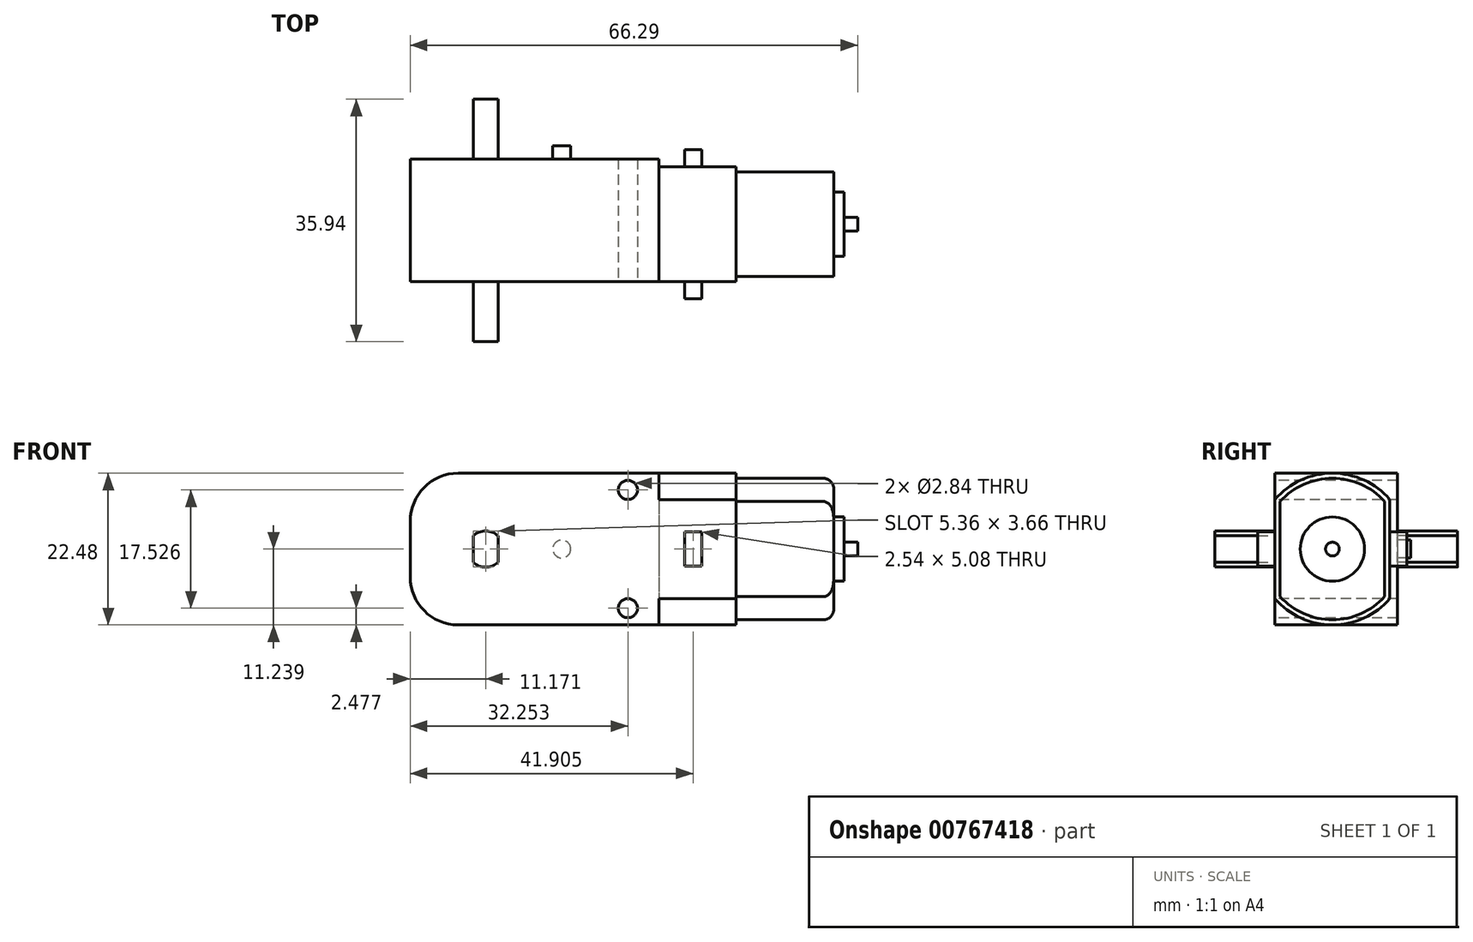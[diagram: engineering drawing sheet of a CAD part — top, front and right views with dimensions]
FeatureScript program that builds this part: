
annotation { "Feature Type Name" : "Feature", "Feature Type Description" : "" }
export const myFeature = defineFeature(function(context is Context, id is Id, definition is map)
    precondition{}
    {
        {
            var Q0;
            Q0=qCreatedBy(makeId("Top.planeOp"),FACE);
            var sketch = newSketch(context, id + "F0", { "sketchPlane" : qUnion([Q0])});
            skLineSegment(sketch, "E0.bottom", {"start": v(49.21, -49.21) * mm, "end": v(-49.21, -49.21) * mm, "construction": true});
            skLineSegment(sketch, "E0.top", {"start": v(49.21, 49.21) * mm, "end": v(-49.21, 49.21) * mm, "construction": true});
            skLineSegment(sketch, "E0.left", {"start": v(49.21, -49.21) * mm, "end": v(49.21, 49.21) * mm, "construction": true});
            skLineSegment(sketch, "E0.right", {"start": v(-49.21, -49.21) * mm, "end": v(-49.21, 49.21) * mm, "construction": true});
            skPoint(sketch, "E0.middle", {"position": v(0, 0) * mm});
            skLineSegment(sketch, "E1", {"start": v(-35.05, -0.76) * mm, "end": v(35.05, -0.76) * mm, "construction": true});
            skLineSegment(sketch, "E2", {"start": v(0, 11.11) * mm, "end": v(0, -11.11) * mm, "construction": true});
            skLineSegment(sketch, "E3", {"start": v(-18.41, 7.75) * mm, "end": v(18.42, 7.75) * mm});
            skLineSegment(sketch, "E4.MirrorCS", {"start": v(-18.41, -9.27) * mm, "end": v(18.41, -9.27) * mm});
            skLineSegment(sketch, "E5", {"start": v(18.42, 7.75) * mm, "end": v(18.42, -9.27) * mm});
            skLineSegment(sketch, "E6.MirrorCS", {"start": v(-18.42, 7.75) * mm, "end": v(-18.41, -9.27) * mm});
            skPoint(sketch, "E7.orphan", {"position": v(12.01, 7.75) * mm});
            skPoint(sketch, "E8.orphan", {"position": v(12.01, -9.27) * mm});
            skPoint(sketch, "E9.orphan", {"position": v(18.42, -26.12) * mm});
            skPoint(sketch, "E10.orphan", {"position": v(-18.41, -26.12) * mm});
            skPoint(sketch, "E11.orphan", {"position": v(-32.46, 7.75) * mm});
            skPoint(sketch, "E12.orphan", {"position": v(-18.42, 15.48) * mm});
            skPoint(sketch, "E13.orphan", {"position": v(18.41, 15.48) * mm});
            skPoint(sketch, "E14.orphan", {"position": v(-32.46, -9.27) * mm});
            skSolve(sketch);
        }
        {
            var Q0;
            Q0=makeQuery(id+"F0.imprint","IMPRINT",FACE,{"disambiguationData":[TD([[makeQuery(id+"F0.imprint","IMPRINT",EDGE,{"derivedFrom":sQuery(id+"F0.wireOp",EDGE,"E3")}),-1.0]])]});
            extrude(context, id + "F1", {"entities" : qUnion([Q0]), "depth" : 22.48 * mm});
        }
        {
            var Q0;
            Q0=makeQuery(id+"F1.opExtrude","CAP_EDGE",EDGE,{"disambiguationData":[OSD([sQuery(id+"F0.wireOp",EDGE,"E6.MirrorCS")])],"isStart":false});
            var Q1;
            Q1=makeQuery(id+"F1.opExtrude","CAP_EDGE",EDGE,{"disambiguationData":[OSD([sQuery(id+"F0.wireOp",EDGE,"E6.MirrorCS")])],"isStart":true});
            fillet(context, id + "F2", {"entities" : qUnion([Q0, Q1]), "radius" : 7.11 * mm, "tangentPropagation" : true, "allowEdgeOverflow" : false});
        }
        {
            var Q0;
            Q0=makeQuery(id+"F1.opExtrude","SWEPT_FACE",FACE,{"disambiguationData":[OSD([sQuery(id+"F0.wireOp",EDGE,"E5")])]});
            var sketch = newSketch(context, id + "F3", { "sketchPlane" : qUnion([Q0])});
            skLineSegment(sketch, "E15", {"start": v(-9.27, 11.24) * mm, "end": v(7.75, 11.24) * mm, "construction": true});
            skArc(sketch, "E16", {"start": v(-9.27, 3.9) * mm, "mid": v(-0.76, 0) * mm, "end": v(7.75, 3.9) * mm});
            skLineSegment(sketch, "E17.0", {"start": v(-9.27, 18.58) * mm, "end": v(-9.27, 3.9) * mm});
            skLineSegment(sketch, "E18.0", {"start": v(7.75, 18.58) * mm, "end": v(7.75, 3.9) * mm});
            skPoint(sketch, "E19.orphan", {"position": v(-9.27, 22.48) * mm});
            skPoint(sketch, "E20.orphan", {"position": v(7.75, 22.48) * mm});
            skArc(sketch, "E21.trimOffspring", {"start": v(7.75, 18.58) * mm, "mid": v(-0.76, 22.48) * mm, "end": v(-9.27, 18.58) * mm});
            skPoint(sketch, "E22.orphan", {"position": v(7.75, 0) * mm});
            skPoint(sketch, "E23.orphan", {"position": v(-9.27, 0) * mm});
            skSolve(sketch);
        }
        {
            var Q0;
            {var subQ1=sQuery(id+"F3.wireOp",EDGE,"E17.0");Q0=makeQuery(id+"F3.imprint","IMPRINT",FACE,{"disambiguationData":[TD([[makeQuery(id+"F3.imprint","IMPRINT",EDGE,{"derivedFrom":subQ1}),1.0]])]});}
            var Q1;
            Q1=makeQuery(id+"F1.opExtrude","SWEPT_FACE",FACE,{"disambiguationData":[OSD([sQuery(id+"F0.wireOp",EDGE,"E6.MirrorCS")])]});
            extrude(context, id + "F4", {"entities" : qUnion([Q0, Q1]), "operationType" : NewBodyOperationType.ADD, "depth" : 27.43 * mm});
        }
        {
            var Q0;
            Q0=makeQuery(id+"F4.opExtrude","CAP_FACE",FACE,{"disambiguationData":[OSD([sQuery(id+"F3.wireOp",EDGE,"E16"),sQuery(id+"F3.wireOp",EDGE,"E17.0"),sQuery(id+"F3.wireOp",EDGE,"E18.0"),sQuery(id+"F3.wireOp",EDGE,"E21.trimOffspring")])],"isStart":false});
            var sketch = newSketch(context, id + "F5", { "sketchPlane" : qUnion([Q0])});
            skLineSegment(sketch, "E24.0", {"start": v(-8.5, 18.3) * mm, "end": v(-8.5, 4.19) * mm});
            skArc(sketch, "E24.1", {"start": v(6.99, 18.3) * mm, "mid": v(-0.76, 21.72) * mm, "end": v(-8.5, 18.3) * mm});
            skLineSegment(sketch, "E24.2", {"start": v(6.99, 4.19) * mm, "end": v(6.99, 18.3) * mm});
            skArc(sketch, "E24.3", {"start": v(-8.5, 4.19) * mm, "mid": v(-0.76, 0.76) * mm, "end": v(6.99, 4.19) * mm});
            skLineSegment(sketch, "E25.0", {"start": v(-14.86, 20.43) * mm, "end": v(-14.86, 2.05) * mm});
            skArc(sketch, "E25.1", {"start": v(13.34, 20.43) * mm, "mid": v(-0.76, 28.07) * mm, "end": v(-14.86, 20.43) * mm});
            skLineSegment(sketch, "E25.2", {"start": v(13.34, 2.05) * mm, "end": v(13.34, 20.43) * mm});
            skArc(sketch, "E25.3", {"start": v(-14.86, 2.05) * mm, "mid": v(-0.76, -5.59) * mm, "end": v(13.34, 2.05) * mm});
            skSolve(sketch);
        }
        {
            var Q0;
            Q0=makeQuery(id+"F5.imprint","IMPRINT",FACE,{"disambiguationData":[TD([[makeQuery(id+"F5.imprint","IMPRINT",EDGE,{"derivedFrom":sQuery(id+"F5.wireOp",EDGE,"E25.0")}),1.0]])]});
            var Q1;
            Q1=makeQuery(id+"F5.imprint","IMPRINT",FACE,{"disambiguationData":[TD([[makeQuery(id+"F5.imprint","IMPRINT",EDGE,{"derivedFrom":sQuery(id+"F5.wireOp",EDGE,"E24.0")}),-1.0]])]});
            extrude(context, id + "F6", {"entities" : qUnion([Q0, Q1]), "operationType" : NewBodyOperationType.REMOVE, "oppositeDirection" : true, "depth" : 16 * mm});
        }
        {
            var Q0;
            Q0=makeQuery(id+"F4.opExtrude","CAP_FACE",FACE,{"disambiguationData":[OSD([sQuery(id+"F3.wireOp",EDGE,"E16"),sQuery(id+"F3.wireOp",EDGE,"E17.0"),sQuery(id+"F3.wireOp",EDGE,"E18.0"),sQuery(id+"F3.wireOp",EDGE,"E21.trimOffspring")])],"isStart":false});
            var sketch = newSketch(context, id + "F7", { "sketchPlane" : qUnion([Q0])});
            skCircle(sketch, "E26", {"center": v(-0.76, 11.24) * mm, "radius": 4.76 * mm});
            skCircle(sketch, "E27", {"center": v(-0.76, 11.24) * mm, "radius": 12.82 * mm});
            skSolve(sketch);
        }
        {
            var Q0;
            Q0=makeQuery(id+"F7.imprint","IMPRINT",FACE,{"disambiguationData":[TD([[makeQuery(id+"F7.imprint","IMPRINT",EDGE,{"derivedFrom":sQuery(id+"F7.wireOp",EDGE,"E27")}),1.0]])]});
            var Q1;
            Q1=makeQuery(id+"F7.imprint","IMPRINT",FACE,{"disambiguationData":[TD([[makeQuery(id+"F7.imprint","IMPRINT",EDGE,{"derivedFrom":sQuery(id+"F7.wireOp",EDGE,"E26")}),-1.0]])]});
            extrude(context, id + "F8", {"entities" : qUnion([Q0, Q1]), "operationType" : NewBodyOperationType.REMOVE, "oppositeDirection" : true, "depth" : 1.52 * mm});
        }
        {
            var Q0;
            Q0=makeQuery(id+"F8.boolean.opBoolean","INTERSECT",EDGE,{"derivedFrom":[makeQuery(id+"F6.boolean.opBoolean","COPY",FACE,{"derivedFrom":makeQuery(id+"F6.opExtrude","SWEPT_FACE",FACE,{"disambiguationData":[OSD([sQuery(id+"F5.wireOp",EDGE,"E24.3")])]})}),makeQuery(id+"F8.opExtrude","CAP_FACE",FACE,{"disambiguationData":[OSD([sQuery(id+"F7.wireOp",EDGE,"E26"),sQuery(id+"F7.wireOp",EDGE,"E27")])],"isStart":false})]});
            var Q1;
            Q1=makeQuery(id+"F8.boolean.opBoolean","INTERSECT",EDGE,{"derivedFrom":[makeQuery(id+"F6.boolean.opBoolean","COPY",FACE,{"derivedFrom":makeQuery(id+"F6.opExtrude","SWEPT_FACE",FACE,{"disambiguationData":[OSD([sQuery(id+"F5.wireOp",EDGE,"E24.1")])]})}),makeQuery(id+"F8.opExtrude","CAP_FACE",FACE,{"disambiguationData":[OSD([sQuery(id+"F7.wireOp",EDGE,"E26"),sQuery(id+"F7.wireOp",EDGE,"E27")])],"isStart":false})]});
            fillet(context, id + "F9", {"entities" : qUnion([Q0, Q1]), "radius" : 1.52 * mm, "tangentPropagation" : true, "allowEdgeOverflow" : false});
        }
        {
            var Q0;
            Q0=makeQuery(id+"F4.opExtrude","CAP_FACE",FACE,{"disambiguationData":[OSD([sQuery(id+"F3.wireOp",EDGE,"E16"),sQuery(id+"F3.wireOp",EDGE,"E17.0"),sQuery(id+"F3.wireOp",EDGE,"E18.0"),sQuery(id+"F3.wireOp",EDGE,"E21.trimOffspring")])],"isStart":false});
            var sketch = newSketch(context, id + "F10", { "sketchPlane" : qUnion([Q0])});
            skCircle(sketch, "E28", {"center": v(-0.76, 11.24) * mm, "radius": 1.02 * mm});
            skSolve(sketch);
        }
        {
            var Q0;
            Q0=makeQuery(id+"F10.imprint","IMPRINT",FACE,{"disambiguationData":[TD([[makeQuery(id+"F10.imprint","IMPRINT",EDGE,{"derivedFrom":sQuery(id+"F10.wireOp",EDGE,"E28")}),1.0]])]});
            extrude(context, id + "F11", {"entities" : qUnion([Q0]), "operationType" : NewBodyOperationType.ADD, "depth" : 2.03 * mm});
        }
        {
            var Q0;
            Q0=makeQuery(id+"F4.boolean.opBoolean","MERGE",FACE,{"derivedFrom":[makeQuery(id+"F1.opExtrude","SWEPT_FACE",FACE,{"disambiguationData":[OSD([sQuery(id+"F0.wireOp",EDGE,"E4.MirrorCS")])]}),makeQuery(id+"F4.opExtrude","SWEPT_FACE",FACE,{"disambiguationData":[OSD([sQuery(id+"F3.wireOp",EDGE,"E17.0")])]})]});
            var sketch = newSketch(context, id + "F12", { "sketchPlane" : qUnion([Q0])});
            skLineSegment(sketch, "E29", {"start": v(29.85, 11.24) * mm, "end": v(18.51, 11.24) * mm, "construction": true});
            skLineSegment(sketch, "E30", {"start": v(22.23, 13.78) * mm, "end": v(22.23, 8.7) * mm});
            skLineSegment(sketch, "E31", {"start": v(24.77, 13.78) * mm, "end": v(24.77, 8.7) * mm});
            skLineSegment(sketch, "E32", {"start": v(22.23, 13.78) * mm, "end": v(24.77, 13.78) * mm});
            skLineSegment(sketch, "E33.MirrorCS", {"start": v(22.23, 8.7) * mm, "end": v(24.77, 8.7) * mm});
            skPoint(sketch, "E34.orphan", {"position": v(19.69, 8.7) * mm});
            skPoint(sketch, "E35.orphan", {"position": v(27.19, 8.7) * mm});
            skPoint(sketch, "E36.orphan", {"position": v(27.19, 13.78) * mm});
            skPoint(sketch, "E37.orphan", {"position": v(19.69, 13.78) * mm});
            skSolve(sketch);
        }
        {
            var Q0;
            Q0=makeQuery(id+"F12.imprint","IMPRINT",FACE,{"disambiguationData":[TD([[makeQuery(id+"F12.imprint","IMPRINT",EDGE,{"derivedFrom":sQuery(id+"F12.wireOp",EDGE,"E30")}),1.0]])]});
            extrude(context, id + "F13", {"entities" : qUnion([Q0]), "operationType" : NewBodyOperationType.ADD, "depth" : 2.54 * mm});
        }
        {
            var Q0;
            Q0=makeQuery(id+"F4.boolean.opBoolean","MERGE",FACE,{"derivedFrom":[makeQuery(id+"F1.opExtrude","SWEPT_FACE",FACE,{"disambiguationData":[OSD([sQuery(id+"F0.wireOp",EDGE,"E3")])]}),makeQuery(id+"F4.opExtrude","SWEPT_FACE",FACE,{"disambiguationData":[OSD([sQuery(id+"F3.wireOp",EDGE,"E18.0")])]})]});
            var sketch = newSketch(context, id + "F14", { "sketchPlane" : qUnion([Q0])});
            skLineSegment(sketch, "E38.0", {"start": v(11.3, 0) * mm, "end": v(-18.42, 0) * mm});
            skArc(sketch, "E39.0", {"start": v(11.3, 0) * mm, "mid": v(16.33, 2.08) * mm, "end": v(18.41, 7.11) * mm});
            skLineSegment(sketch, "E40.0", {"start": v(18.42, 15.37) * mm, "end": v(18.42, 7.11) * mm});
            skArc(sketch, "E41.0", {"start": v(18.41, 15.37) * mm, "mid": v(16.33, 20.4) * mm, "end": v(11.3, 22.48) * mm});
            skLineSegment(sketch, "E42.0", {"start": v(11.3, 22.48) * mm, "end": v(-18.42, 22.48) * mm});
            skLineSegment(sketch, "E43", {"start": v(-18.42, 22.48) * mm, "end": v(-18.42, 0) * mm});
            skSolve(sketch);
        }
        {
            var Q0;
            {var subQ0=sQuery(id+"F14.wireOp",EDGE,"E38.0");Q0=makeQuery(id+"F14.imprint","IMPRINT",FACE,{"disambiguationData":[TD([[makeQuery(id+"F14.imprint","IMPRINT",EDGE,{"derivedFrom":subQ0}),-1.0]])]});}
            extrude(context, id + "F15", {"entities" : qUnion([Q0]), "operationType" : NewBodyOperationType.ADD, "depth" : 1.14 * mm});
        }
        {
            var Q0;
            Q0=makeQuery(id+"F4.boolean.opBoolean","MERGE",FACE,{"derivedFrom":[makeQuery(id+"F1.opExtrude","SWEPT_FACE",FACE,{"disambiguationData":[OSD([sQuery(id+"F0.wireOp",EDGE,"E3")])]}),makeQuery(id+"F4.opExtrude","SWEPT_FACE",FACE,{"disambiguationData":[OSD([sQuery(id+"F3.wireOp",EDGE,"E18.0")])]})]});
            var sketch = newSketch(context, id + "F16", { "sketchPlane" : qUnion([Q0])});
            skLineSegment(sketch, "E44.0.0", {"start": v(-24.77, 13.78) * mm, "end": v(-22.23, 13.78) * mm});
            skLineSegment(sketch, "E44.0.1", {"start": v(-22.23, 13.78) * mm, "end": v(-22.23, 8.7) * mm});
            skLineSegment(sketch, "E44.0.2", {"start": v(-22.23, 8.7) * mm, "end": v(-24.77, 8.7) * mm});
            skLineSegment(sketch, "E44.0.3", {"start": v(-24.77, 8.7) * mm, "end": v(-24.77, 13.78) * mm});
            skSolve(sketch);
        }
        {
            var Q0;
            Q0=makeQuery(id+"F16.imprint","IMPRINT",FACE,{"disambiguationData":[TD([[makeQuery(id+"F16.imprint","IMPRINT",EDGE,{"derivedFrom":sQuery(id+"F16.wireOp",EDGE,"E44.0.0")}),-1.0]])]});
            extrude(context, id + "F17", {"entities" : qUnion([Q0]), "operationType" : NewBodyOperationType.ADD, "depth" : 2.54 * mm});
        }
        {
            var Q0;
            Q0=makeQuery(id+"F4.boolean.opBoolean","MERGE",FACE,{"derivedFrom":[makeQuery(id+"F1.opExtrude","SWEPT_FACE",FACE,{"disambiguationData":[OSD([sQuery(id+"F0.wireOp",EDGE,"E4.MirrorCS")])]}),makeQuery(id+"F4.opExtrude","SWEPT_FACE",FACE,{"disambiguationData":[OSD([sQuery(id+"F3.wireOp",EDGE,"E17.0")])]})]});
            var sketch = newSketch(context, id + "F18", { "sketchPlane" : qUnion([Q0])});
            skArc(sketch, "E45", {"start": v(-5.41, 13.2) * mm, "mid": v(-7.24, 13.92) * mm, "end": v(-9.07, 13.2) * mm});
            skPoint(sketch, "E45.centerSnap0", {"position": v(-18.41, 11.24) * mm});
            skLineSegment(sketch, "E46", {"start": v(-9.07, 13.2) * mm, "end": v(-9.07, 9.28) * mm});
            skLineSegment(sketch, "E47", {"start": v(-5.41, 13.2) * mm, "end": v(-5.41, 9.28) * mm});
            skPoint(sketch, "E48.orphan", {"position": v(-9.07, 5.55) * mm});
            skArc(sketch, "E49.trimOffspring", {"start": v(-9.07, 9.28) * mm, "mid": v(-7.24, 8.56) * mm, "end": v(-5.41, 9.28) * mm});
            skSolve(sketch);
        }
        {
            var Q0;
            Q0=makeQuery(id+"F18.imprint","IMPRINT",FACE,{"disambiguationData":[TD([[makeQuery(id+"F18.imprint","IMPRINT",EDGE,{"derivedFrom":sQuery(id+"F18.wireOp",EDGE,"E45")}),1.0]])]});
            extrude(context, id + "F19", {"entities" : qUnion([Q0]), "operationType" : NewBodyOperationType.ADD, "depth" : 8.9 * mm});
        }
        {
            var Q0;
            Q0=makeQuery(id+"F15.opExtrude","CAP_FACE",FACE,{"disambiguationData":[OSD([sQuery(id+"F14.wireOp",EDGE,"E38.0"),sQuery(id+"F14.wireOp",EDGE,"E39.0"),sQuery(id+"F14.wireOp",EDGE,"E40.0"),sQuery(id+"F14.wireOp",EDGE,"E41.0"),sQuery(id+"F14.wireOp",EDGE,"E42.0"),sQuery(id+"F14.wireOp",EDGE,"E43")])],"isStart":false});
            var sketch = newSketch(context, id + "F20", { "sketchPlane" : qUnion([Q0])});
            skLineSegment(sketch, "E50.0.0", {"start": v(5.41, 9.28) * mm, "end": v(5.41, 13.2) * mm});
            skArc(sketch, "E50.0.1", {"start": v(5.41, 13.2) * mm, "mid": v(7.24, 13.92) * mm, "end": v(9.07, 13.2) * mm});
            skLineSegment(sketch, "E50.0.2", {"start": v(9.07, 13.2) * mm, "end": v(9.07, 9.28) * mm});
            skArc(sketch, "E50.0.3", {"start": v(9.07, 9.28) * mm, "mid": v(7.24, 8.56) * mm, "end": v(5.41, 9.28) * mm});
            skSolve(sketch);
        }
        {
            var Q0;
            Q0=makeQuery(id+"F20.imprint","IMPRINT",FACE,{"disambiguationData":[TD([[makeQuery(id+"F20.imprint","IMPRINT",EDGE,{"derivedFrom":sQuery(id+"F20.wireOp",EDGE,"E50.0.0")}),-1.0]])]});
            extrude(context, id + "F21", {"entities" : qUnion([Q0]), "operationType" : NewBodyOperationType.ADD, "depth" : 8.9 * mm});
        }
        {
            var Q0;
            Q0=makeQuery(id+"F15.opExtrude","CAP_FACE",FACE,{"disambiguationData":[OSD([sQuery(id+"F14.wireOp",EDGE,"E38.0"),sQuery(id+"F14.wireOp",EDGE,"E39.0"),sQuery(id+"F14.wireOp",EDGE,"E40.0"),sQuery(id+"F14.wireOp",EDGE,"E41.0"),sQuery(id+"F14.wireOp",EDGE,"E42.0"),sQuery(id+"F14.wireOp",EDGE,"E43")])],"isStart":false});
            var sketch = newSketch(context, id + "F22", { "sketchPlane" : qUnion([Q0])});
            skLineSegment(sketch, "E51", {"start": v(7.24, 13.92) * mm, "end": v(7.24, 8.56) * mm, "construction": true});
            skLineSegment(sketch, "E52", {"start": v(-4.04, 11.24) * mm, "end": v(-4.04, 17.91) * mm, "construction": true});
            skLineSegment(sketch, "E53", {"start": v(18.42, 11.24) * mm, "end": v(0, 11.24) * mm, "construction": true});
            skCircle(sketch, "E54", {"center": v(-4.04, 11.24) * mm, "radius": 1.32 * mm});
            skSolve(sketch);
        }
        {
            var Q0;
            Q0=makeQuery(id+"F22.imprint","IMPRINT",FACE,{"disambiguationData":[TD([[makeQuery(id+"F22.imprint","IMPRINT",EDGE,{"derivedFrom":sQuery(id+"F22.wireOp",EDGE,"E54")}),1.0]])]});
            extrude(context, id + "F23", {"entities" : qUnion([Q0]), "operationType" : NewBodyOperationType.ADD, "depth" : 1.96 * mm});
        }
        {
            var Q0;
            Q0=makeQuery(id+"F4.boolean.opBoolean","MERGE",FACE,{"derivedFrom":[makeQuery(id+"F1.opExtrude","SWEPT_FACE",FACE,{"disambiguationData":[OSD([sQuery(id+"F0.wireOp",EDGE,"E4.MirrorCS")])]}),makeQuery(id+"F4.opExtrude","SWEPT_FACE",FACE,{"disambiguationData":[OSD([sQuery(id+"F3.wireOp",EDGE,"E17.0")])]})]});
            var sketch = newSketch(context, id + "F24", { "sketchPlane" : qUnion([Q0])});
            skCircle(sketch, "E55", {"center": v(13.84, 20) * mm, "radius": 1.42 * mm});
            skLineSegment(sketch, "E56", {"start": v(-5.41, 11.24) * mm, "end": v(15.76, 11.24) * mm, "construction": true});
            skCircle(sketch, "E57.MirrorC", {"center": v(13.84, 2.48) * mm, "radius": 1.42 * mm});
            skSolve(sketch);
        }
        {
            var Q0;
            Q0=qSketchRegion(id+"F24",true);
            extrude(context, id + "F25", {"entities" : qUnion([Q0]), "operationType" : NewBodyOperationType.REMOVE, "oppositeDirection" : true, "depth" : 25.4 * mm});
        }
    });
